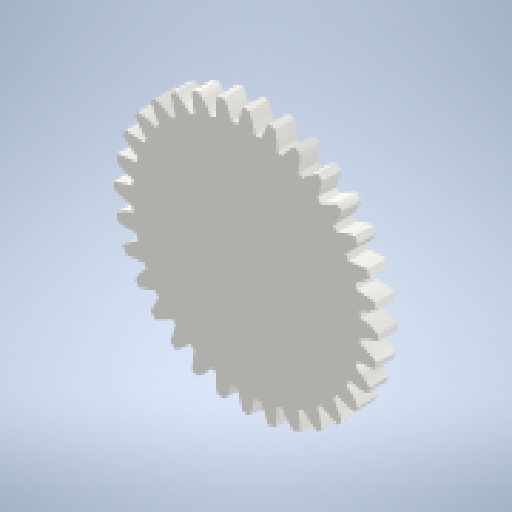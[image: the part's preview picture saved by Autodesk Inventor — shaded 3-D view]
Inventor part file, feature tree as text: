
AUTODESK INVENTOR PART (.ipt)
format: ipt  version: 2024 (Build 280153000, 153)  size: 291,840 bytes
history: native  units: mm (DEFAULTED — no unit token found)
features: plane x3, other x3, extrude x2, sketch x2
ambient origin geometry x8: Origin, YZ Plane, XZ Plane, XY Plane, X Axis, Y Axis, Z Axis, Center Point
bodies: Solid1 (feature_tree)
feature tree (10):
  extrude  "Extrusion1"  Depth=5.0mm TaperAngle=0.0deg
  plane  "Work Plane2"
  plane  "Work Plane8"
  plane  "Work Plane9"
  other  "Spur Gear"
  extrude  "Extrusion2"  Depth=10.0mm TaperAngle=0.0deg
  sketch  "Sketch1"  dims[d0=68.0mm d1=5.0mm d2=0.0mm]
  other  "Srf1"
  sketch  "Sketch3"  dims[d3=64.0mm d4=10.0mm d5=0.0mm d16=42.0mm d17=0.0mm d34=0.981748mm d39=0.0mm d41=0.0mm d43=42.0mm d46=42.0mm d47=0.0mm d48=0.0mm d49=3.0mm d50=10.0mm d51=0.0mm]
  other  "Pitch Diameter"
